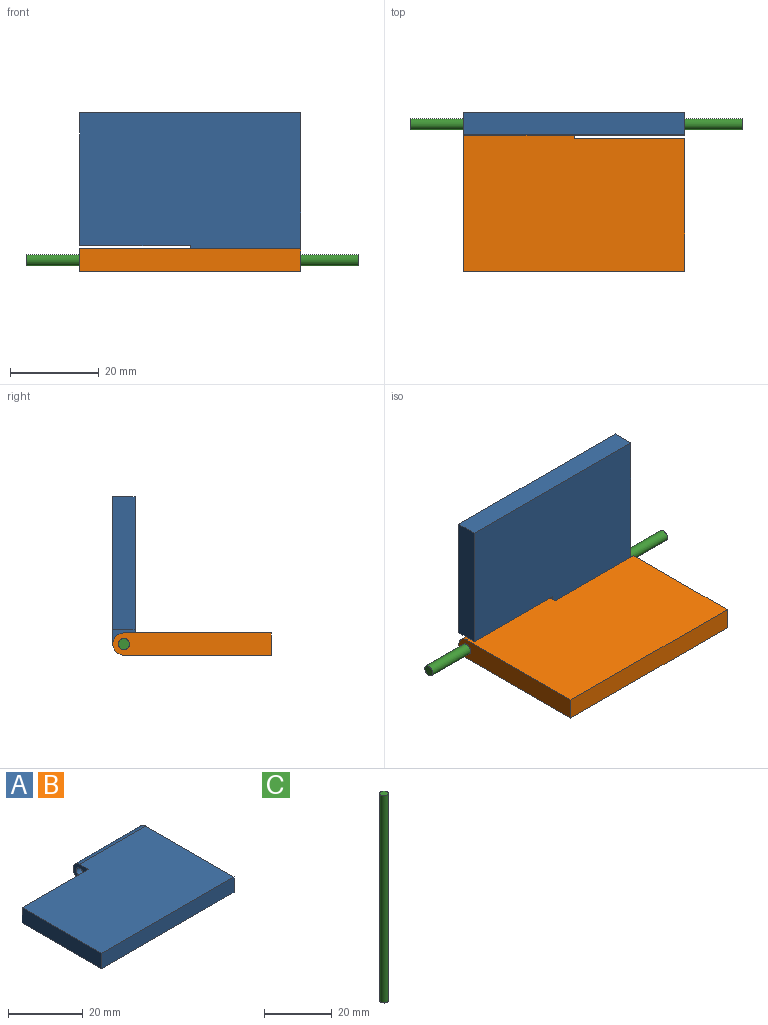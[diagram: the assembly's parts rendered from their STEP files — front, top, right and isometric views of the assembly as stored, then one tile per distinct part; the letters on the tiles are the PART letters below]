
ASSEMBLY  parts=3 mates=5
PART A: 9 faces, bbox 50x35.8x5 mm
  f0: plane 25x5mm, normal (0,1,0), area 125mm2, adj f1,f4,f5,f8
  f1: plane 30x5mm, normal (-1,0,0), area 150mm2, adj f0,f2,f4,f5
  f2: plane 50x5mm, normal (0,-1,0), area 250mm2, adj f1,f3,f4,f5
  f3: plane 35.75x5mm, normal (1,0,0), area 171.2mm2, adj f2,f4,f5,f6,f7
  f4: plane 50x33.25mm, normal (0,0,1), area 1581.3mm2, adj f0,f1,f2,f3,f6,f8
  f5: plane 50x33.25mm, normal (0,0,-1), area 1581.3mm2, adj f0,f1,f2,f3,f6,f8
  f6: cylinder r=2.5mm len=25mm, axis (-1,0,0), area 196.3mm2, adj f3,f4,f5,f8
  f7: cylinder r=1.25mm len=25mm, axis (-1,0,0), area 196.3mm2, adj f3,f8
  f8: plane 5.75x5mm, normal (-1,0,0), area 21.2mm2, adj f0,f4,f5,f6,f7
PART B: same geometry as A
PART C: 3 faces, bbox 2.5x2.5x75 mm
  f0: cylinder r=1.25mm len=75mm, axis (0,0,-1), area 589mm2, adj f1,f2
  f1: plane 2.5x2.5mm, normal (0,0,1), area 4.9mm2, adj f0
  f2: plane 2.5x2.5mm, normal (0,0,-1), area 4.9mm2, adj f0
PLACE A rot(axis=(-1,0,0),90deg) t=(-20.54,21.99,-9.42)mm
PLACE B rot(axis=(0,1,0),180deg) t=(-20.54,3.74,-27.67)mm
PLACE C rot(axis=(0.58,0.58,0.58),120deg) t=(-57.66,21.99,-27.67)mm
MATE planar A.f7 <-> B.f8  axis (-1,0,0) through (-20.54,21.99,-27.67)mm
MATE parallel A.f5 <-> B.f0  axis (0,-1,0) through (-19.9,19.49,-10.28)mm
MATE cylindrical C.f0 <-> A.f7  axis (-1,0,0) through (-20.16,21.99,-27.67)mm
MATE slider A.f7 <-> B.f7  axis (-1,0,0) through (-8.04,21.99,-27.67)mm
MATE parallel B.f5 <-> A.f0  axis (0,0,1) through (-21.19,4.6,-25.17)mm
